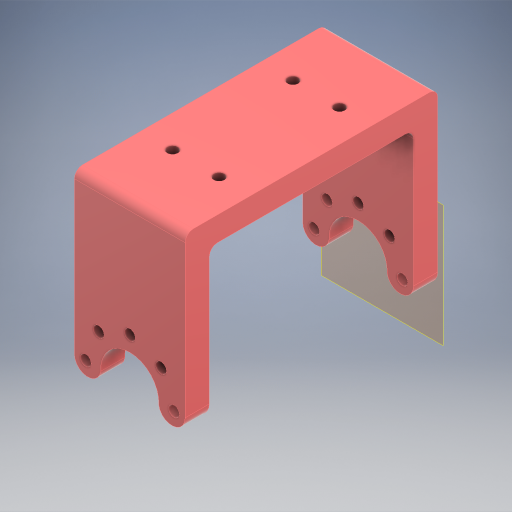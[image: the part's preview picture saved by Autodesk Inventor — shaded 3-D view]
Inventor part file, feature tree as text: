
AUTODESK INVENTOR PART (.ipt)
format: ipt  version: 2024 (Build 280153000, 153)  size: 389,120 bytes
history: native  units: in
note: dims shown in document units (in); Inventor stores cm internally (conversion verified against a paired STEP export)
features: extrude x9, sketch x9, other x7, reference x2, projected_geometry x2, fillet x1, mirror x1
ambient origin geometry x8: Origin, YZ Plane, XZ Plane, XY Plane, X Axis, Y Axis, Z Axis, Center Point
bodies: Body1 (feature_tree)
feature tree (31):
  other  "솔리드1"
  other  "작업 평면1"
  extrude  "돌출1"  Depth=0.5709in
  extrude  "돌출2"  Depth=0.1063in
  extrude  "돌출3"  Depth=0.1063in
  extrude  "돌출4"  Depth=0.1063in
  extrude  "돌출5"  Depth=0.1063in
  extrude  "돌출6"  Depth=0.1063in
  extrude  "돌출7"  Depth=0.7874in
  extrude  "돌출8"  Depth=0.2362in
  extrude  "돌출9"  Depth=0.2362in
  fillet  "모깎기1"  Radius=0.2362in
  mirror  "미러1"
  sketch  "스케치1"
  reference  "참조1"
  sketch  "스케치2"
  sketch  "스케치3"
  reference  "참조2"
  sketch  "스케치4"
  sketch  "스케치5"
  sketch  "스케치6"
  sketch  "스케치7"
  sketch  "스케치8"
  projected_geometry  "투영된 루프1"
  sketch  "스케치9"
  projected_geometry  "투영된 루프2"
  other  "조립품7"
  other  "64아이들러:2"
  other  "HN05-i1:1"
  other  "MX-106T+idle.ipt:2"
  other  "MX-106T:1"
